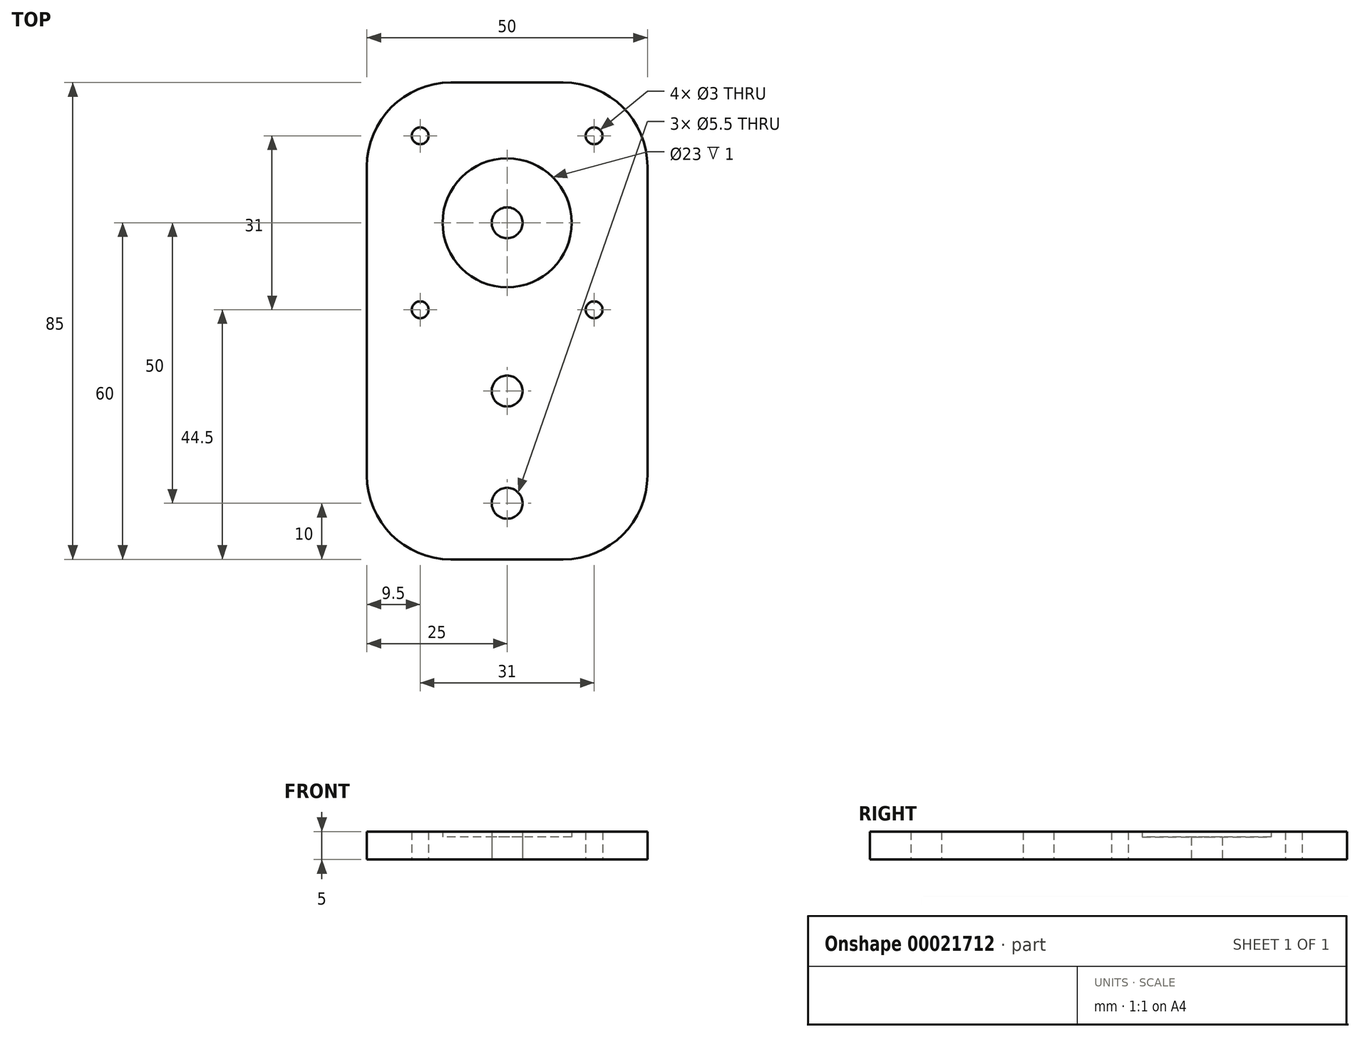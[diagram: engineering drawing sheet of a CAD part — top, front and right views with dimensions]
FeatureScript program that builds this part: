
annotation { "Feature Type Name" : "Feature", "Feature Type Description" : "" }
export const myFeature = defineFeature(function(context is Context, id is Id, definition is map)
    precondition{}
    {
        {
            var Q0;
            Q0=qCreatedBy(makeId("Top.planeOp"),FACE);
            var sketch = newSketch(context, id + "F0", { "sketchPlane" : qUnion([Q0])});
            skLineSegment(sketch, "E0.bottom", {"start": v(0, 0) * mm, "end": v(25, 0) * mm, "construction": true});
            skLineSegment(sketch, "E0.top", {"start": v(0, 25) * mm, "end": v(10, 25) * mm});
            skLineSegment(sketch, "E0.left", {"start": v(0, 0) * mm, "end": v(0, 25) * mm, "construction": true});
            skLineSegment(sketch, "E0.right", {"start": v(25, 0) * mm, "end": v(25, 10) * mm});
            skCircle(sketch, "E1", {"center": v(0, 0) * mm, "radius": 2.75 * mm});
            skCircle(sketch, "E2", {"center": v(0, 0) * mm, "radius": 11.5 * mm});
            skCircle(sketch, "E3", {"center": v(15.5, 15.5) * mm, "radius": 1.5 * mm});
            skCircle(sketch, "E4", {"center": v(0, -30) * mm, "radius": 2.75 * mm});
            skCircle(sketch, "E5", {"center": v(0, -50) * mm, "radius": 2.75 * mm});
            skLineSegment(sketch, "E6", {"start": v(15.5, 0) * mm, "end": v(15.5, 15.5) * mm, "construction": true});
            skLineSegment(sketch, "E7", {"start": v(0, 0) * mm, "end": v(0, -30) * mm, "construction": true});
            skLineSegment(sketch, "E8", {"start": v(0, -50) * mm, "end": v(0, -30) * mm, "construction": true});
            skLineSegment(sketch, "E9.MirrorCS", {"start": v(0, 25) * mm, "end": v(-10, 25) * mm});
            skCircle(sketch, "E10.MirrorC", {"center": v(-15.5, 15.5) * mm, "radius": 1.5 * mm});
            skLineSegment(sketch, "E11.MirrorCS", {"start": v(-25, 0) * mm, "end": v(-25, 10) * mm});
            skLineSegment(sketch, "E12.MirrorCS", {"start": v(25, 0) * mm, "end": v(25, -25) * mm});
            skLineSegment(sketch, "E13.MirrorCS", {"start": v(-25, 0) * mm, "end": v(-25, -25) * mm});
            skCircle(sketch, "E14.MirrorC", {"center": v(-15.5, -15.5) * mm, "radius": 1.5 * mm});
            skCircle(sketch, "E15.MirrorC", {"center": v(15.5, -15.5) * mm, "radius": 1.5 * mm});
            skLineSegment(sketch, "E16", {"start": v(-25, -25) * mm, "end": v(-25, -45) * mm});
            skLineSegment(sketch, "E17", {"start": v(-10, -60) * mm, "end": v(10, -60) * mm});
            skLineSegment(sketch, "E18", {"start": v(25, -25) * mm, "end": v(25, -45) * mm});
            skPoint(sketch, "E19.visualSharp", {"position": v(-25, 25) * mm});
            skArc(sketch, "E19.filletArc", {"start": v(-10, 25) * mm, "mid": v(-20.6, 20.6) * mm, "end": v(-25, 10) * mm});
            skPoint(sketch, "E20.visualSharp", {"position": v(25, 25) * mm});
            skArc(sketch, "E20.filletArc", {"start": v(25, 10) * mm, "mid": v(20.6, 20.6) * mm, "end": v(10, 25) * mm});
            skPoint(sketch, "E21.visualSharp", {"position": v(25, -60) * mm});
            skArc(sketch, "E21.filletArc", {"start": v(10, -60) * mm, "mid": v(20.6, -55.6) * mm, "end": v(25, -45) * mm});
            skPoint(sketch, "E22.visualSharp", {"position": v(-25, -60) * mm});
            skArc(sketch, "E22.filletArc", {"start": v(-25, -45) * mm, "mid": v(-20.6, -55.6) * mm, "end": v(-10, -60) * mm});
            skSolve(sketch);
        }
        {
            var Q0;
            Q0=makeQuery(id+"F0.imprint","IMPRINT",FACE,{"disambiguationData":[TD([[makeQuery(id+"F0.imprint","IMPRINT",EDGE,{"derivedFrom":sQuery(id+"F0.wireOp",EDGE,"E0.top")}),-1.0]])]});
            extrude(context, id + "F1", {"entities" : qUnion([Q0]), "depth" : 5 * mm});
        }
        {
            var Q0;
            Q0=makeQuery(id+"F0.imprint","IMPRINT",FACE,{"disambiguationData":[TD([[makeQuery(id+"F0.imprint","IMPRINT",EDGE,{"derivedFrom":sQuery(id+"F0.wireOp",EDGE,"E1")}),-1.0]])]});
            extrude(context, id + "F2", {"entities" : qUnion([Q0]), "operationType" : NewBodyOperationType.ADD, "depth" : 4 * mm});
        }
    });
